# Revit family: PRD_AR_CntrTpWshBsns_QUADROTopCountertopWashbasin_ANMT4002
name_source: partatom
category: Plumbing Fixtures
revit_build: Autodesk Revit 2018 (Build: 20190510_1515(x64)
units: mm (PartAtom-declared; Revit-internal decimal feet)

## family parameters
Cut with Voids When Loaded = No
Host = Face
OmniClass Number = 23.45.05.14.14
OmniClass Title = Sinks/Lavatories
Part Type = Normal
Room Calculation Point = No
Round Connector Dimension = Use Diameter
Shared = No

## types (1)
- ANMT4002
    AssetType = Fixed
    BIMObjectName = PRD_AR_CounterTopWashBasins_QUADROTopCountertopWashbasin_ANMT4002
    BowlDepth = 355.00 mm
    BowlHeight = 100.00 mm
    BowlPosition = Center
    BowlShape = Rectangle
    BowlWidth = 535.00 mm
    Category = Pr_40_20_96_18, Countertop washbasins
    Color = alpine white
    Default Elevation = 850 mm  [stored 2.78871 ft]
    Description = QUADROtop countertop basin, made of MIRANIT resin-bonded mineral material with pore-free, alpine white smooth surface (temperature-resistant up to 80°C). Rectangular shape with rounded edges and seamless bowl, with overflow. No silicone sealant is required due to the invisible seal which is integrated in to the mounting edge. Drilling templates and mounting materials included. Bowl dimensions 535 x 100 x 355 mm (W x H x D).
    DiameterNominal = 32 mm
    DrainSize = 32 mm  [stored 0.104987 ft]
    DurationUnit = year
    Features = mineral material, alpine white smooth surface, rectangular shape
    Finish = smooth
    Flow = 0.0 L/s
    GrossWeight = 25.50 kg
    IfcExportAs = IfcSanitaryTerminalType
    IfcExportType = WASHHANDBASIN
    IntegralAccessories = incl. drilling templates and mounting materials
    Manufacturer = KWC Group AG
    ManufacturerName = KWC Group AG
    ManufacturerURL = www.kwc.com
    Material = mineral material
    MaterialCode = Miranit
    Model = ANMT4002
    ModelNumber = 2030054383
    ModelReference = ANMT4002
    MountingOffset = 140 mm  [stored 0.459318 ft]
    NBSDescription = Counter top wash basins
    NBSReference = 45-35-70/360
    Name = Countertop Washbasin ANMT4002
    NetWeight = 18.00 kg
    NominalDepth = 380 mm
    NominalHeight = 140 mm  [stored 0.459318 ft]
    NominalWidth = 550 mm
    NumberOfBowls = 1
    Overflow = Yes
    OverflowPosition = Back
    ProductInformation = https://pim.kwc.com
    Shape = rectangular
    SiphonIncluded = No
    Size = 550 x 140 x 380 mm (W x H x D)
    Spillway = Yes
    Splashback = No
    TailorMade = No
    TapLedge = No
    TypeOfBasin = Vanity basin
    TypeOfMounting = Table mounting
    URL = www.kwc.com
    Uniclass2015Code = Pr_40_20_96_18
    Uniclass2015Title = Countertop washbasins
    Uniclass2015Version = Products v1.17
    Version = 1
    WarrantyDurationUnit = year
    WashbasinMaterial = PRD_AR_Miranit_Alpinewhite
    WasteHolePosition = Center
    WasteHoleProjection = 160.00 mm
    WasteKitIncluded = No
    WasteSize = DN 32

note: [stored X ft] marks values corroborated as IEEE doubles in the binary element streams (Revit-internal decimal feet)

## geometry (parser evidence)
native form markers: Sweep x8
no freeform markers — native parametric forms only
